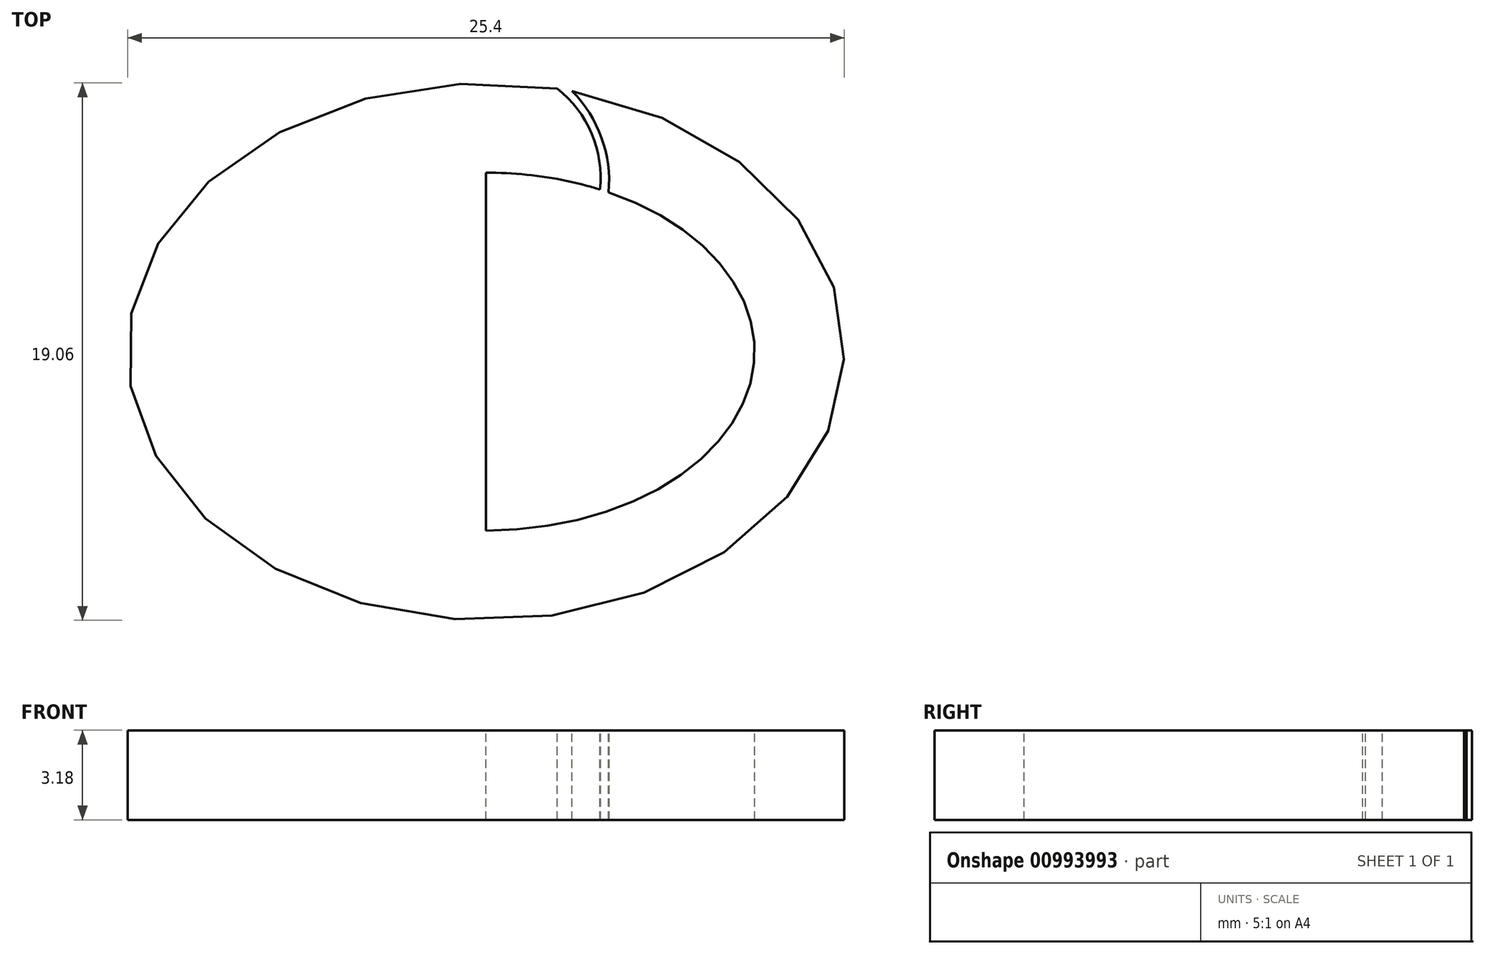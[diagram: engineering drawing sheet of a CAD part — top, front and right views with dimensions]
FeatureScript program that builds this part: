
annotation { "Feature Type Name" : "Feature", "Feature Type Description" : "" }
export const myFeature = defineFeature(function(context is Context, id is Id, definition is map)
    precondition{}
    {
        {
            var Q0;
            Q0=qCreatedBy(makeId("Top.planeOp"),FACE);
            var sketch = newSketch(context, id + "F0", { "sketchPlane" : qUnion([Q0])});
            skEllipse(sketch, "E0", {"center": v(0, 0) * mm, "majorRadius": 12.7 * mm, "minorRadius": 9.53 * mm, "majorAxis": v(-1, 0)});
            skSolve(sketch);
        }
        {
            var Q0;
            Q0 = qSketchRegion(id + "F0", true);
            extrude(context, id + "F1", {"entities" : qUnion([Q0]), "depth" : 3.17 * mm, "offsetDistance" : 25.4 * mm});
        }
        {
            var Q0;
            Q0=makeQuery(id+"F1.opExtrude","CAP_FACE",FACE,{"disambiguationData":[OSD([sQuery(id+"F0.wireOp",EDGE,"E0")])],"isStart":false});
            var sketch = newSketch(context, id + "F2", { "sketchPlane" : qUnion([Q0])});
            skEllipse(sketch, "E1", {"center": v(0, 0) * mm, "majorRadius": 9.53 * mm, "minorRadius": 6.35 * mm, "majorAxis": v(1, 0)});
            skSolve(sketch);
        }
        {
            var Q0;
            Q0 = qSketchRegion(id + "F2", true);
            extrude(context, id + "F3", {"entities" : qUnion([Q0]), "operationType" : NewBodyOperationType.REMOVE, "oppositeDirection" : true, "depth" : 25.4 * mm, "offsetDistance" : 25.4 * mm});
        }
        {
            var Q0;
            Q0=qCreatedBy(makeId("Top.planeOp"),FACE);
            var sketch = newSketch(context, id + "F4", { "sketchPlane" : qUnion([Q0])});
            skLineSegment(sketch, "E2", {"start": v(0, 8.14) * mm, "end": v(-10.23, 4.09) * mm});
            skLineSegment(sketch, "E3", {"start": v(-10.23, 4.09) * mm, "end": v(-10.23, -2.78) * mm});
            skLineSegment(sketch, "E4", {"start": v(-10.23, -2.78) * mm, "end": v(0, -8.91) * mm});
            skLineSegment(sketch, "E5", {"start": v(0, -8.91) * mm, "end": v(0, 8.14) * mm});
            skSolve(sketch);
        }
        {
            var Q0;
            Q0 = qSketchRegion(id + "F4", true);
            extrude(context, id + "F5", {"entities" : qUnion([Q0]), "operationType" : NewBodyOperationType.ADD, "depth" : 3.17 * mm, "offsetDistance" : 25.4 * mm});
        }
        {
            var Q0;
            Q0=makeQuery(id+"F5.boolean.opBoolean","MERGE",FACE,{"derivedFrom":[makeQuery(id+"F1.opExtrude","CAP_FACE",FACE,{"disambiguationData":[OSD([sQuery(id+"F0.wireOp",EDGE,"E0")])],"isStart":false}),makeQuery(id+"F5.opExtrude","CAP_FACE",FACE,{"disambiguationData":[OSD([sQuery(id+"F4.wireOp",EDGE,"E2"),sQuery(id+"F4.wireOp",EDGE,"E3"),sQuery(id+"F4.wireOp",EDGE,"E4"),sQuery(id+"F4.wireOp",EDGE,"E5")])],"isStart":false})]});
            var sketch = newSketch(context, id + "F6", { "sketchPlane" : qUnion([Q0])});
            skArc(sketch, "E6", {"start": v(4.04, 5.75) * mm, "mid": v(3.75, 7.74) * mm, "end": v(2.53, 9.33) * mm});
            skArc(sketch, "E7", {"start": v(4.35, 5.65) * mm, "mid": v(4.1, 7.59) * mm, "end": v(3.06, 9.25) * mm});
            skArc(sketch, "E8", {"start": v(3.06, 9.25) * mm, "mid": v(2.82, 9.43) * mm, "end": v(2.53, 9.33) * mm});
            skArc(sketch, "E9", {"start": v(4.04, 5.75) * mm, "mid": v(4.16, 5.6) * mm, "end": v(4.35, 5.65) * mm});
            skSolve(sketch);
        }
        {
            var Q0;
            Q0 = qSketchRegion(id + "F6", true);
            extrude(context, id + "F7", {"entities" : qUnion([Q0]), "operationType" : NewBodyOperationType.REMOVE, "oppositeDirection" : true, "depth" : 25.4 * mm, "offsetDistance" : 25.4 * mm});
        }
    });
